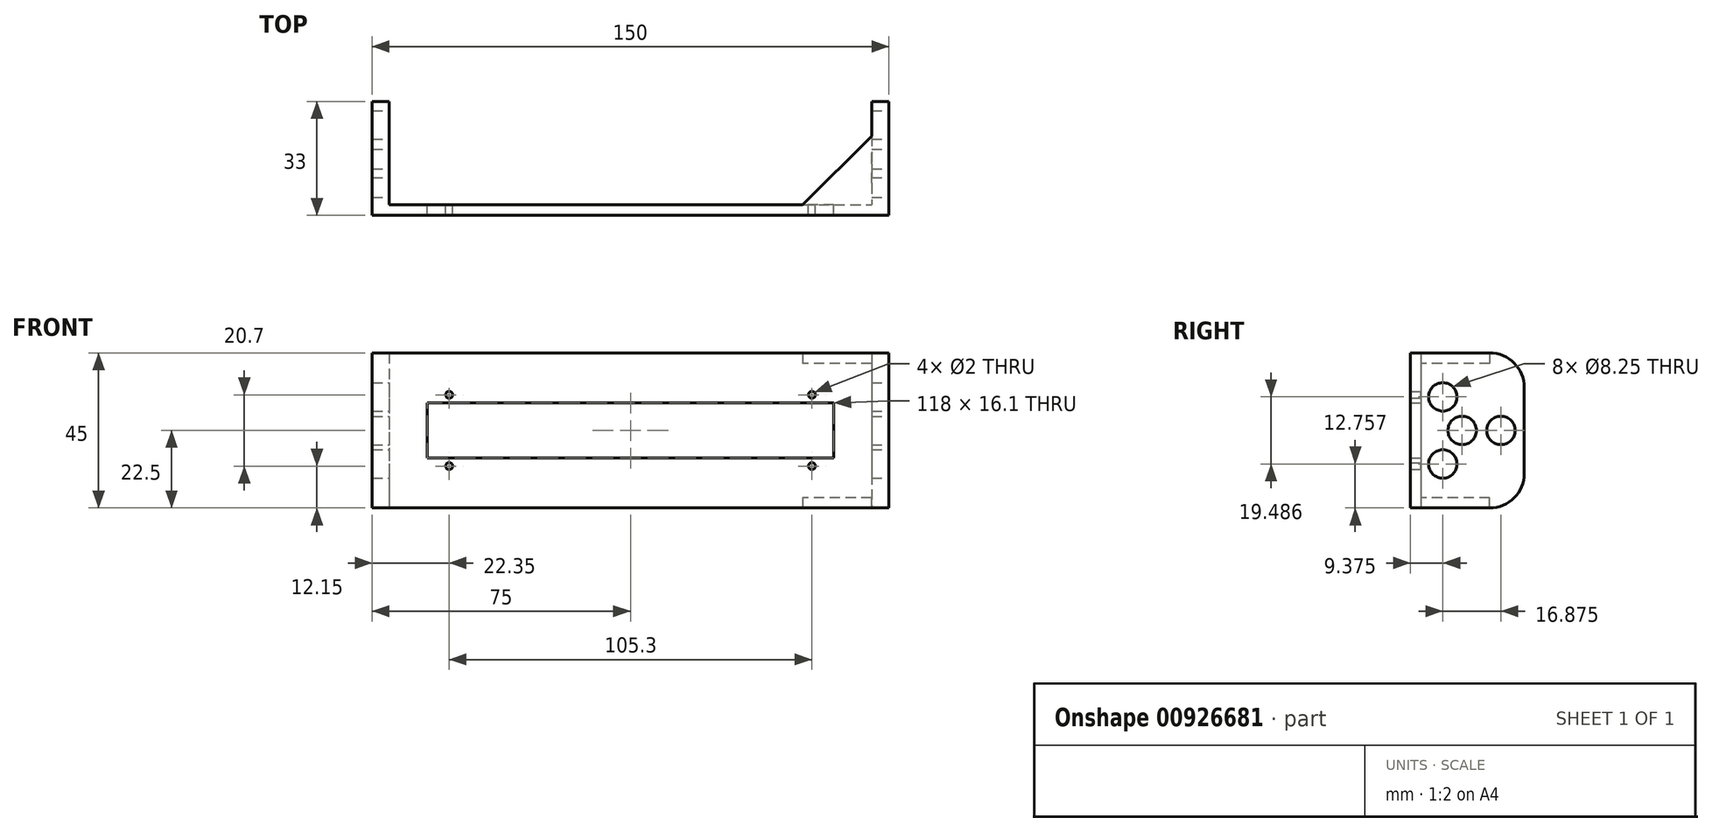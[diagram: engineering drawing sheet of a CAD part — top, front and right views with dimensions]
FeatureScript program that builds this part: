
annotation { "Feature Type Name" : "Feature", "Feature Type Description" : "" }
export const myFeature = defineFeature(function(context is Context, id is Id, definition is map)
    precondition{}
    {
        {
            var Q0;
            Q0=qCreatedBy(makeId("Front.planeOp"),FACE);
            var sketch = newSketch(context, id + "F0", { "sketchPlane" : qUnion([Q0])});
            skLineSegment(sketch, "E0.bottom", {"start": v(59, 8.05) * mm, "end": v(-59, 8.05) * mm});
            skLineSegment(sketch, "E0.top", {"start": v(59, -8.05) * mm, "end": v(-59, -8.05) * mm});
            skLineSegment(sketch, "E0.left", {"start": v(59, 8.05) * mm, "end": v(59, -8.05) * mm});
            skLineSegment(sketch, "E0.right", {"start": v(-59, 8.05) * mm, "end": v(-59, -8.05) * mm});
            skPoint(sketch, "E0.middle", {"position": v(0, 0) * mm});
            skLineSegment(sketch, "E1.bottom", {"start": v(52.65, 10.35) * mm, "end": v(-52.65, 10.35) * mm, "construction": true});
            skLineSegment(sketch, "E1.top", {"start": v(52.65, -10.35) * mm, "end": v(-52.65, -10.35) * mm, "construction": true});
            skLineSegment(sketch, "E1.left", {"start": v(52.65, 10.35) * mm, "end": v(52.65, -10.35) * mm, "construction": true});
            skLineSegment(sketch, "E1.right", {"start": v(-52.65, 10.35) * mm, "end": v(-52.65, -10.35) * mm, "construction": true});
            skLineSegment(sketch, "E2.bottom", {"start": v(75, -22.5) * mm, "end": v(-75, -22.5) * mm});
            skLineSegment(sketch, "E2.top", {"start": v(75, 22.5) * mm, "end": v(-75, 22.5) * mm});
            skLineSegment(sketch, "E2.left", {"start": v(75, -22.5) * mm, "end": v(75, 22.5) * mm});
            skLineSegment(sketch, "E2.right", {"start": v(-75, -22.5) * mm, "end": v(-75, 22.5) * mm});
            skCircle(sketch, "E3", {"center": v(-52.65, 10.35) * mm, "radius": 1 * mm});
            skCircle(sketch, "E4", {"center": v(-52.65, -10.35) * mm, "radius": 1 * mm});
            skCircle(sketch, "E5", {"center": v(52.65, 10.35) * mm, "radius": 1 * mm});
            skCircle(sketch, "E6", {"center": v(52.65, -10.35) * mm, "radius": 1 * mm});
            skSolve(sketch);
        }
        {
            var Q0;
            Q0 = qSketchRegion(id + "F0", true);
            extrude(context, id + "F1", {"entities" : qUnion([Q0]), "depth" : 3 * mm, "offsetDistance" : 25.4 * mm});
        }
        {
            var Q0;
            Q0=makeQuery(id+"F1.opExtrude","CAP_FACE",FACE,{"disambiguationData":[OSD([sQuery(id+"F0.wireOp",EDGE,"E0.bottom"),sQuery(id+"F0.wireOp",EDGE,"E0.top"),sQuery(id+"F0.wireOp",EDGE,"E0.left"),sQuery(id+"F0.wireOp",EDGE,"E0.right"),sQuery(id+"F0.wireOp",EDGE,"E2.bottom"),sQuery(id+"F0.wireOp",EDGE,"E2.top"),sQuery(id+"F0.wireOp",EDGE,"E2.left"),sQuery(id+"F0.wireOp",EDGE,"E2.right"),sQuery(id+"F0.wireOp",EDGE,"E3"),sQuery(id+"F0.wireOp",EDGE,"E4"),sQuery(id+"F0.wireOp",EDGE,"E5"),sQuery(id+"F0.wireOp",EDGE,"E6")])],"isStart":true});
            var sketch = newSketch(context, id + "F2", { "sketchPlane" : qUnion([Q0])});
            skLineSegment(sketch, "E7.bottom", {"start": v(-75, 22.5) * mm, "end": v(-70, 22.5) * mm});
            skLineSegment(sketch, "E7.top", {"start": v(-75, -22.5) * mm, "end": v(-70, -22.5) * mm});
            skLineSegment(sketch, "E7.left", {"start": v(-75, 22.5) * mm, "end": v(-75, -22.5) * mm});
            skLineSegment(sketch, "E7.right", {"start": v(-70, 22.5) * mm, "end": v(-70, -22.5) * mm});
            skLineSegment(sketch, "E8.bottom", {"start": v(75, 22.5) * mm, "end": v(70, 22.5) * mm});
            skLineSegment(sketch, "E8.top", {"start": v(75, -22.5) * mm, "end": v(70, -22.5) * mm});
            skLineSegment(sketch, "E8.left", {"start": v(75, 22.5) * mm, "end": v(75, -22.5) * mm});
            skLineSegment(sketch, "E8.right", {"start": v(70, 22.5) * mm, "end": v(70, -22.5) * mm});
            skSolve(sketch);
        }
        {
            var Q0;
            Q0 = qSketchRegion(id + "F2", true);
            extrude(context, id + "F3", {"entities" : qUnion([Q0]), "operationType" : NewBodyOperationType.ADD, "depth" : 30 * mm, "offsetDistance" : 25 * mm});
        }
        {
            var Q0;
            Q0=makeQuery(id+"F3.boolean.opBoolean","MERGE",FACE,{"derivedFrom":[makeQuery(id+"F1.opExtrude","SWEPT_FACE",FACE,{"disambiguationData":[OSD([sQuery(id+"F0.wireOp",EDGE,"E2.left")])]}),makeQuery(id+"F3.opExtrude","SWEPT_FACE",FACE,{"disambiguationData":[OSD([sQuery(id+"F2.wireOp",EDGE,"E7.left")])]})]});
            var sketch = newSketch(context, id + "F4", { "sketchPlane" : qUnion([Q0])});
            skCircle(sketch, "E9", {"center": v(12, 0) * mm, "radius": 4.12 * mm});
            skCircle(sketch, "E10.1.0.0", {"center": v(23.25, 0) * mm, "radius": 4.12 * mm});
            skLineSegment(sketch, "E10.direction1", {"start": v(12, 0) * mm, "end": v(23.25, 0) * mm, "construction": true});
            skCircle(sketch, "E11.1.0", {"center": v(6.38, 9.74) * mm, "radius": 4.12 * mm});
            skCircle(sketch, "E11.2.0", {"center": v(6.38, -9.74) * mm, "radius": 4.12 * mm});
            skLineSegment(sketch, "E12", {"start": v(0, 22.5) * mm, "end": v(30, 22.5) * mm});
            skLineSegment(sketch, "E13", {"start": v(0, 22.5) * mm, "end": v(0, 22.5) * mm});
            skLineSegment(sketch, "E14", {"start": v(0, -22.5) * mm, "end": v(0, -22.5) * mm});
            skLineSegment(sketch, "E15", {"start": v(0, -22.5) * mm, "end": v(30, -22.5) * mm});
            skLineSegment(sketch, "E16", {"start": v(30, -22.5) * mm, "end": v(30, 22.5) * mm});
            skLineSegment(sketch, "E17", {"start": v(30, 22.5) * mm, "end": v(30, 22.5) * mm});
            skLineSegment(sketch, "E18", {"start": v(30, -22.5) * mm, "end": v(30, -22.5) * mm});
            skSolve(sketch);
        }
        {
            var Q0;
            Q0 = qSketchRegion(id + "F4", true);
            extrude(context, id + "F5", {"entities" : qUnion([Q0]), "operationType" : NewBodyOperationType.REMOVE, "oppositeDirection" : true, "depth" : 541 * mm, "offsetDistance" : 25 * mm});
        }
        {
            var Q0;
            Q0=makeQuery(id+"F3.opExtrude","CAP_EDGE",EDGE,{"disambiguationData":[OSD([sQuery(id+"F2.wireOp",EDGE,"E7.bottom")])],"isStart":false});
            var Q1;
            Q1=makeQuery(id+"F3.opExtrude","CAP_EDGE",EDGE,{"disambiguationData":[OSD([sQuery(id+"F2.wireOp",EDGE,"E7.top")])],"isStart":false});
            var Q2;
            Q2=makeQuery(id+"F3.opExtrude","CAP_EDGE",EDGE,{"disambiguationData":[OSD([sQuery(id+"F2.wireOp",EDGE,"E8.bottom")])],"isStart":false});
            var Q3;
            Q3=makeQuery(id+"F3.opExtrude","CAP_EDGE",EDGE,{"disambiguationData":[OSD([sQuery(id+"F2.wireOp",EDGE,"E8.top")])],"isStart":false});
            fillet(context, id + "F6", {"entities" : qUnion([Q0, Q1, Q2, Q3]), "radius" : 10 * mm, "tangentPropagation" : true, "allowEdgeOverflow" : false});
        }
        {
            var Q0;
            Q0=makeQuery(id+"F3.opExtrude","SWEPT_FACE",FACE,{"disambiguationData":[OSD([sQuery(id+"F2.wireOp",EDGE,"E7.right")])]});
            var sketch = newSketch(context, id + "F7", { "sketchPlane" : qUnion([Q0])});
            skLineSegment(sketch, "E19.top", {"start": v(-20, 19.5) * mm, "end": v(0, 19.5) * mm});
            skLineSegment(sketch, "E19.left", {"start": v(-20, 22.5) * mm, "end": v(-20, 19.5) * mm});
            skLineSegment(sketch, "E19.right", {"start": v(0, 22.5) * mm, "end": v(0, 19.5) * mm});
            skLineSegment(sketch, "E20.MirrorCS", {"start": v(-20, -19.5) * mm, "end": v(0, -19.5) * mm});
            skLineSegment(sketch, "E21.MirrorCS", {"start": v(-20, -22.5) * mm, "end": v(-20, -19.5) * mm});
            skLineSegment(sketch, "E22.MirrorCS", {"start": v(-20, -22.5) * mm, "end": v(0, -22.5) * mm});
            skLineSegment(sketch, "E23.MirrorCS", {"start": v(0, -22.5) * mm, "end": v(0, -19.5) * mm});
            skLineSegment(sketch, "E24.1", {"start": v(-20, 22.5) * mm, "end": v(0, 22.5) * mm});
            skSolve(sketch);
        }
        {
            var Q0;
            Q0 = qSketchRegion(id + "F7", true);
            extrude(context, id + "F8", {"entities" : qUnion([Q0]), "operationType" : NewBodyOperationType.ADD, "depth" : 20 * mm, "offsetDistance" : 25 * mm});
        }
        {
            var Q0;
            Q0=makeQuery(id+"F8.boolean.opBoolean","MERGE",FACE,{"derivedFrom":[makeQuery(id+"F3.boolean.opBoolean","MERGE",FACE,{"derivedFrom":[makeQuery(id+"F1.opExtrude","SWEPT_FACE",FACE,{"disambiguationData":[OSD([sQuery(id+"F0.wireOp",EDGE,"E2.top")])]}),makeQuery(id+"F3.opExtrude","SWEPT_FACE",FACE,{"disambiguationData":[OSD([sQuery(id+"F2.wireOp",EDGE,"E7.bottom")])]}),makeQuery(id+"F3.opExtrude","SWEPT_FACE",FACE,{"disambiguationData":[OSD([sQuery(id+"F2.wireOp",EDGE,"E8.bottom")])]})]}),makeQuery(id+"F8.opExtrude","SWEPT_FACE",FACE,{"disambiguationData":[OSD([sQuery(id+"F7.wireOp",EDGE,"E24.1")])]})]});
            var sketch = newSketch(context, id + "F9", { "sketchPlane" : qUnion([Q0])});
            skLineSegment(sketch, "E25", {"start": v(70, 20) * mm, "end": v(50, 0) * mm});
            skLineSegment(sketch, "E26", {"start": v(70, 20) * mm, "end": v(50, 20) * mm});
            skLineSegment(sketch, "E27", {"start": v(50, 0) * mm, "end": v(50, 20) * mm});
            skSolve(sketch);
        }
        {
            var Q0;
            Q0 = qSketchRegion(id + "F9", true);
            extrude(context, id + "F10", {"entities" : qUnion([Q0]), "operationType" : NewBodyOperationType.REMOVE, "endBound" : BoundingType.THROUGH_ALL, "oppositeDirection" : true, "depth" : 25 * mm, "offsetDistance" : 25 * mm});
        }
    });
